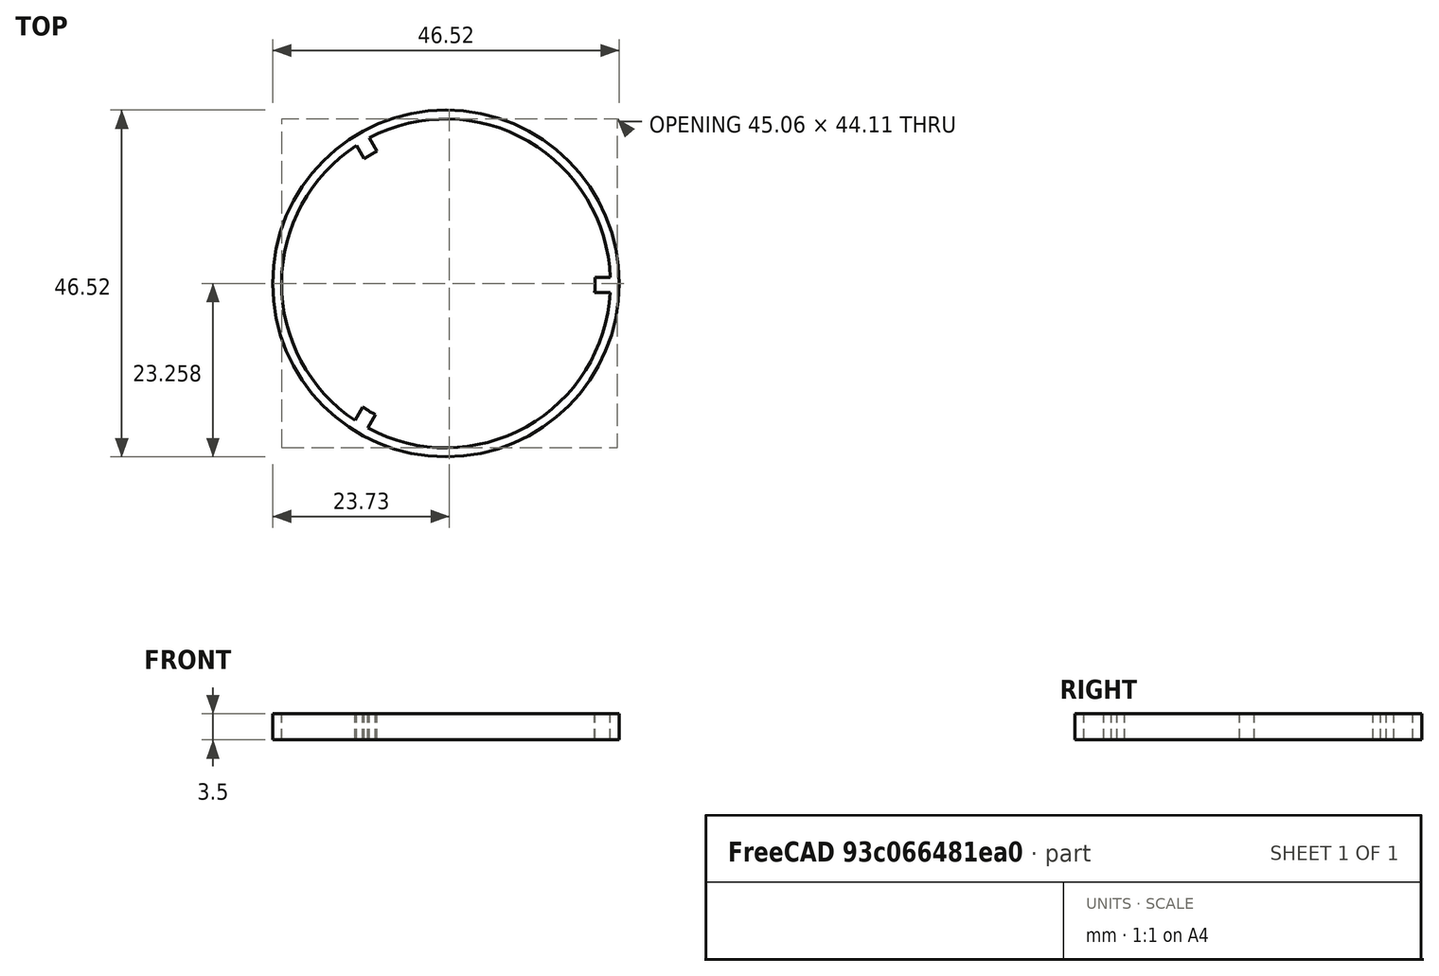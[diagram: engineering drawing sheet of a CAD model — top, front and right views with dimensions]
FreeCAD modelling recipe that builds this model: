
FCSTD DOCUMENT  (FreeCAD 0.16R6712 (Git))
Label: out-ring
License: All rights reserved
LicenseURL: http://en.wikipedia.org/wiki/All_rights_reserved
objects: Part::FeaturePython×5, Part::Cylinder×3, Part::Box×3
note: 11 computed .brp shape members not serialized (recipe doc carries the construction recipe); baked Part::Feature solids carry a one-line shape summary decoded from their .brp

FEATURE [Part::Cylinder] Cylinder  label="圆柱体"
  Angle = 360
  Height = 3.5
  Radius = 23.26
FEATURE [Part::Box] Box010  label="立方体007"
  Height = 3.5
  Length = 23
  Placement = pos=(0,-1.2,-32) rot=(0,0,1;0rad)
  Width = 2
FEATURE [Part::Box] Box011  label="立方体008"
  Height = 3.5
  Length = 23
  Placement = pos=(1,0,-32) rot=(0,0,1;2.0944rad)
  Width = 2
FEATURE [Part::Box] Box012  label="立方体009"
  Height = 3.5
  Length = 23
  Placement = pos=(-1,1,-32) rot=(0,0,-1;2.0944rad)
  Width = 2
FEATURE [Part::FeaturePython] Connect  # WARN: FeaturePython — macro-defined, semantics opaque (R4)
  Base = -> Box010
  Mode = 1
  Tool = -> Box011
FEATURE [Part::FeaturePython] Connect001  # WARN: FeaturePython — macro-defined, semantics opaque (R4)
  Base = -> Connect
  Mode = 1
  Placement = pos=(0,0,32) rot=(0,0,1;0rad)
  Tool = -> Box012
FEATURE [Part::Cylinder] Cylinder001  label="圆柱体001"
  Angle = 360
  Height = 7
  Placement = pos=(0,0,-3) rot=(0,0,1;0rad)
  Radius = 22.06
FEATURE [Part::FeaturePython] Cutout  # WARN: FeaturePython — macro-defined, semantics opaque (R4)
  Base = -> Cylinder
  Mode = 3
  Tool = -> Cylinder001
FEATURE [Part::Cylinder] Cylinder002  label="圆柱体002"
  Angle = 360
  Height = 10
  Radius = 20
FEATURE [Part::FeaturePython] Connect002  # WARN: FeaturePython — macro-defined, semantics opaque (R4)
  Base = -> Connect001
  Mode = 1
  Tool = -> Cutout
FEATURE [Part::FeaturePython] Cutout001  # WARN: FeaturePython — macro-defined, semantics opaque (R4)
  Base = -> Connect002
  Mode = 3
  Tool = -> Cylinder002
